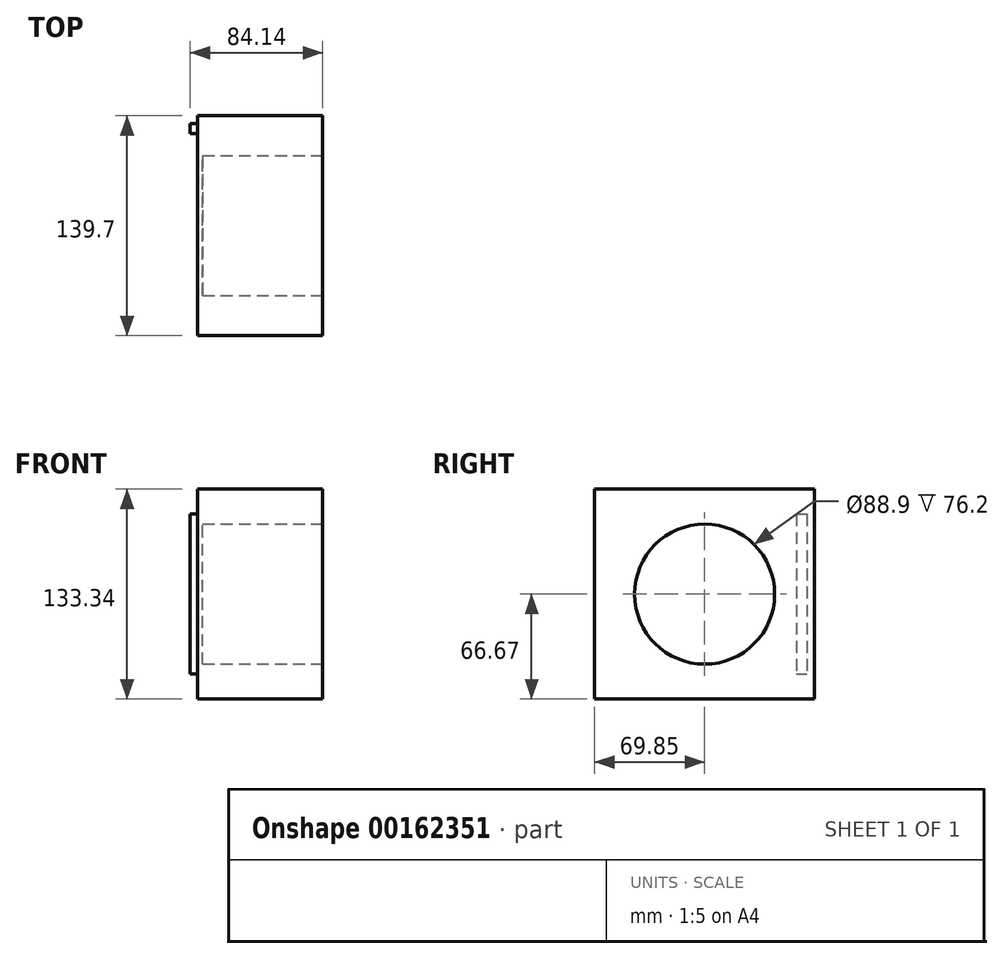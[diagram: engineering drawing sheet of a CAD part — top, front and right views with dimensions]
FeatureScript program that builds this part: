
annotation { "Feature Type Name" : "Feature", "Feature Type Description" : "" }
export const myFeature = defineFeature(function(context is Context, id is Id, definition is map)
    precondition{}
    {
        {
            var Q0;
            Q0=qCreatedBy(makeId("Front.planeOp"),FACE);
            var sketch = newSketch(context, id + "F0", { "sketchPlane" : qUnion([Q0])});
            skLineSegment(sketch, "E0.bottom", {"start": v(39.69, -66.68) * mm, "end": v(-39.69, -66.68) * mm});
            skLineSegment(sketch, "E0.top", {"start": v(39.69, 66.67) * mm, "end": v(-39.69, 66.67) * mm});
            skLineSegment(sketch, "E0.left", {"start": v(39.69, -66.68) * mm, "end": v(39.69, 66.68) * mm});
            skLineSegment(sketch, "E0.right", {"start": v(-39.69, -66.68) * mm, "end": v(-39.69, 66.68) * mm});
            skPoint(sketch, "E0.middle", {"position": v(0, 0) * mm});
            skSolve(sketch);
        }
        {
            var Q0;
            Q0=makeQuery(id+"F0.imprint","IMPRINT",FACE,{"disambiguationData":[TD([[makeQuery(id+"F0.imprint","IMPRINT",EDGE,{"derivedFrom":sQuery(id+"F0.wireOp",EDGE,"E0.bottom")}),-1.0]])]});
            var Q1;
            Q1 = qSketchRegion(id + "F4", true);
            extrude(context, id + "F1", {"entities" : qUnion([Q0, Q1]), "depth" : 139.7 * mm});
        }
        {
            var Q0;
            Q0=makeQuery(id+"F1.opExtrude","SWEPT_FACE",FACE,{"disambiguationData":[OSD([sQuery(id+"F0.wireOp",EDGE,"E0.left")])]});
            var sketch = newSketch(context, id + "F2", { "sketchPlane" : qUnion([Q0])});
            skCircle(sketch, "E1", {"center": v(-69.85, 0) * mm, "radius": 44.45 * mm});
            skPoint(sketch, "E2.startSnap0", {"position": v(-139.7, 0) * mm});
            skSolve(sketch);
        }
        {
            var Q0;
            Q0=makeQuery(id+"F2.imprint","IMPRINT",FACE,{"disambiguationData":[TD([[makeQuery(id+"F2.imprint","IMPRINT",EDGE,{"derivedFrom":sQuery(id+"F2.wireOp",EDGE,"E1")}),1.0]])]});
            extrude(context, id + "F3", {"entities" : qUnion([Q0]), "operationType" : NewBodyOperationType.REMOVE, "oppositeDirection" : true, "depth" : 76.2 * mm});
        }
        {
            var Q0;
            Q0=qCreatedBy(makeId("Right.planeOp"),FACE);
            var sketch = newSketch(context, id + "F4", { "sketchPlane" : qUnion([Q0])});
            skLineSegment(sketch, "E3.bottom", {"start": v(-5.07, -50.8) * mm, "end": v(-11.42, -50.8) * mm});
            skLineSegment(sketch, "E3.top", {"start": v(-5.07, 50.8) * mm, "end": v(-11.42, 50.8) * mm});
            skLineSegment(sketch, "E3.left", {"start": v(-5.07, -50.8) * mm, "end": v(-5.07, 50.8) * mm});
            skLineSegment(sketch, "E3.right", {"start": v(-11.42, -50.8) * mm, "end": v(-11.42, 50.8) * mm});
            skPoint(sketch, "E3.middle", {"position": v(-8.24, 0) * mm});
            skSolve(sketch);
        }
        {
            var Q0;
            Q0 = qSketchRegion(id + "F4", true);
            extrude(context, id + "F5", {"entities" : qUnion([Q0]), "operationType" : NewBodyOperationType.ADD, "oppositeDirection" : true, "depth" : 44.45 * mm});
        }
    });
